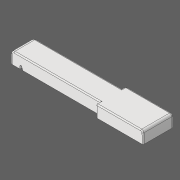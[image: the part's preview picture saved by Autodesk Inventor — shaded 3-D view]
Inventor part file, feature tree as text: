
AUTODESK INVENTOR PART (.ipt)
format: ipt  version: 2020 (Build 240168000, 168)  size: 281,088 bytes
history: native  units: in
note: dims shown in document units (in); Inventor stores cm internally (conversion verified against a paired STEP export)
features: extrude x4, other x3, fillet x2
ambient origin geometry x8: Origin, YZ Plane, XZ Plane, XY Plane, X Axis, Y Axis, Z Axis, Center Point
bodies: Solid1 (feature_tree)
feature tree (9):
  other  "Slot Start Plane"
  other  "Key Profile"
  extrude  "Upper"  TaperAngle=0.0deg  [1 undecoded]
  extrude  "Lower"  TaperAngle=0.0deg  [1 undecoded]
  extrude  "Protrusion Cutout"  Depth=0.0591in
  fillet  "Front Fillet"  Radius=0.1374in
  extrude  "Slot"  [1 undecoded]
  fillet  "Edge Softening"  Radius=0.0787in
  other  "Slot Sketch"
note: 3 required parameter values undecoded (feature->parameter linkage not recoverable at this tier; creation-order binding heuristic only, values carry confidence <= 0.55)
